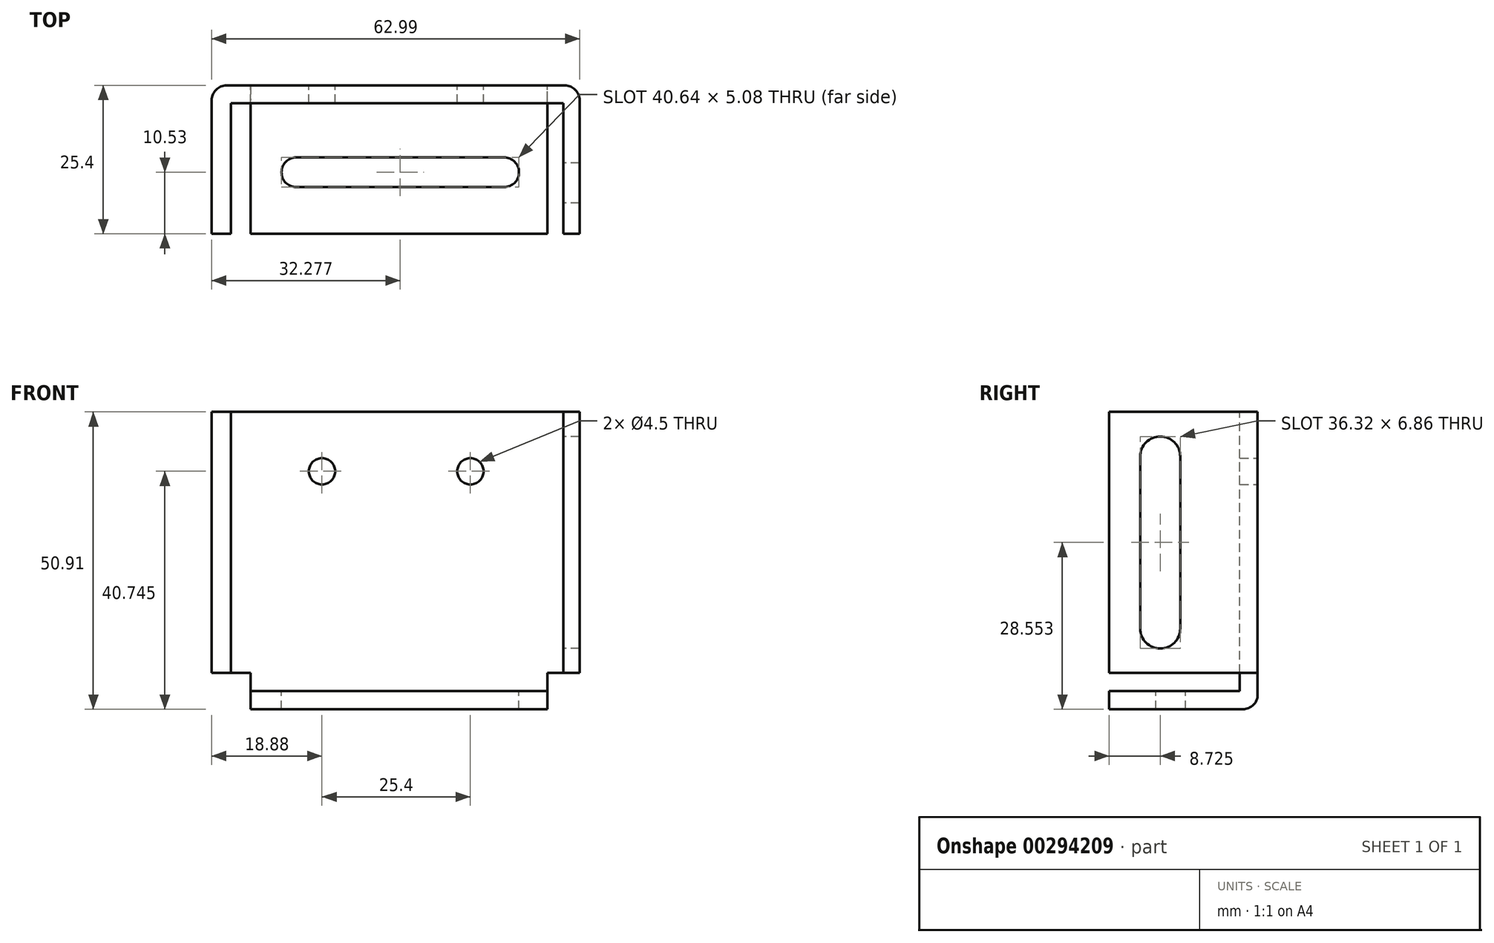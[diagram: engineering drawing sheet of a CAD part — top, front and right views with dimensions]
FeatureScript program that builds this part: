
annotation { "Feature Type Name" : "Feature", "Feature Type Description" : "" }
export const myFeature = defineFeature(function(context is Context, id is Id, definition is map)
    precondition{}
    {
        {
            var Q0;
            Q0=qCreatedBy(makeId("Front.planeOp"),FACE);
            var sketch = newSketch(context, id + "F0", { "sketchPlane" : qUnion([Q0])});
            skLineSegment(sketch, "E0", {"start": v(-29.68, 28.29) * mm, "end": v(33.31, 28.29) * mm});
            skLineSegment(sketch, "E1", {"start": v(33.31, 28.29) * mm, "end": v(33.31, -16.42) * mm});
            skLineSegment(sketch, "E2", {"start": v(33.31, -16.42) * mm, "end": v(27.77, -16.42) * mm});
            skLineSegment(sketch, "E3", {"start": v(27.77, -16.42) * mm, "end": v(27.77, -22.62) * mm});
            skLineSegment(sketch, "E4", {"start": v(27.77, -22.62) * mm, "end": v(-23.03, -22.62) * mm});
            skLineSegment(sketch, "E5", {"start": v(-23.03, -22.62) * mm, "end": v(-23.03, -16.42) * mm});
            skLineSegment(sketch, "E6", {"start": v(-23.03, -16.42) * mm, "end": v(-29.68, -16.42) * mm});
            skLineSegment(sketch, "E7", {"start": v(-29.68, -16.42) * mm, "end": v(-29.68, 28.29) * mm});
            skCircle(sketch, "E8", {"center": v(-10.8, 18.13) * mm, "radius": 2.25 * mm});
            skCircle(sketch, "E9", {"center": v(14.6, 18.13) * mm, "radius": 2.25 * mm});
            skLineSegment(sketch, "E10", {"start": v(-23.03, -19.52) * mm, "end": v(27.77, -19.52) * mm});
            skLineSegment(sketch, "E11", {"start": v(-26.35, -16.42) * mm, "end": v(-26.35, 28.29) * mm});
            skLineSegment(sketch, "E12", {"start": v(30.54, -16.42) * mm, "end": v(30.54, 28.29) * mm});
            skSolve(sketch);
        }
        {
            var Q0;
            Q0=makeQuery(id+"F0.imprint","IMPRINT",FACE,{"disambiguationData":[TD([[makeQuery(id+"F0.imprint","IMPRINT",EDGE,{"derivedFrom":sQuery(id+"F0.wireOp",EDGE,"E8")}),-1.0]])]});
            extrude(context, id + "F1", {"entities" : qUnion([Q0]), "depth" : 3.05 * mm});
        }
        {
            var Q0;
            {var subQ0=sQuery(id+"F0.wireOp",EDGE,"E4");Q0=makeQuery(id+"F0.imprint","IMPRINT",FACE,{"disambiguationData":[TD([[makeQuery(id+"F0.imprint","IMPRINT",EDGE,{"derivedFrom":subQ0}),-1.0]])]});}
            var Q1;
            {var subQ0=sQuery(id+"F0.wireOp",EDGE,"E7");Q1=makeQuery(id+"F0.imprint","IMPRINT",FACE,{"disambiguationData":[TD([[makeQuery(id+"F0.imprint","IMPRINT",EDGE,{"derivedFrom":subQ0}),-1.0]])]});}
            var Q2;
            {var subQ0=sQuery(id+"F0.wireOp",EDGE,"E1");Q2=makeQuery(id+"F0.imprint","IMPRINT",FACE,{"disambiguationData":[TD([[makeQuery(id+"F0.imprint","IMPRINT",EDGE,{"derivedFrom":subQ0}),-1.0]])]});}
            extrude(context, id + "F2", {"entities" : qUnion([Q0, Q1, Q2]), "operationType" : NewBodyOperationType.ADD, "depth" : 25.4 * mm});
        }
        {
            var Q0;
            Q0=makeQuery(id+"F2.opExtrude","SWEPT_FACE",FACE,{"disambiguationData":[OSD([sQuery(id+"F0.wireOp",EDGE,"E10")])]});
            var sketch = newSketch(context, id + "F3", { "sketchPlane" : qUnion([Q0])});
            skLineSegment(sketch, "E13", {"start": v(-15.18, -17.4) * mm, "end": v(20.38, -17.4) * mm});
            skLineSegment(sketch, "E14", {"start": v(-15.18, -12.33) * mm, "end": v(20.38, -12.33) * mm});
            skArc(sketch, "E15", {"start": v(-15.18, -12.33) * mm, "mid": v(-17.72, -14.87) * mm, "end": v(-15.18, -17.4) * mm});
            skArc(sketch, "E16", {"start": v(20.38, -17.4) * mm, "mid": v(22.92, -14.87) * mm, "end": v(20.38, -12.33) * mm});
            skSolve(sketch);
        }
        {
            var Q0;
            Q0=makeQuery(id+"F1.opExtrude","CAP_EDGE",EDGE,{"disambiguationData":[OSD([sQuery(id+"F0.wireOp",EDGE,"E10")])],"isStart":false});
            var Q1;
            Q1=makeQuery(id+"F2.opExtrude","CAP_EDGE",EDGE,{"disambiguationData":[OSD([sQuery(id+"F0.wireOp",EDGE,"E4")])],"isStart":true});
            var Q2;
            Q2=makeQuery(id+"F2.opExtrude","CAP_EDGE",EDGE,{"disambiguationData":[OSD([sQuery(id+"F0.wireOp",EDGE,"E1")])],"isStart":true});
            var Q3;
            Q3=makeQuery(id+"F1.opExtrude","CAP_EDGE",EDGE,{"disambiguationData":[OSD([sQuery(id+"F0.wireOp",EDGE,"E12")])],"isStart":false});
            var Q4;
            Q4=makeQuery(id+"F1.opExtrude","CAP_EDGE",EDGE,{"disambiguationData":[OSD([sQuery(id+"F0.wireOp",EDGE,"E11")])],"isStart":false});
            var Q5;
            Q5=makeQuery(id+"F2.opExtrude","CAP_EDGE",EDGE,{"disambiguationData":[OSD([sQuery(id+"F0.wireOp",EDGE,"E7")])],"isStart":true});
            fillet(context, id + "F4", {"entities" : qUnion([Q0, Q1, Q2, Q3, Q4, Q5]), "radius" : 2.54 * mm, "tangentPropagation" : true, "allowEdgeOverflow" : false});
        }
        {
            var Q0;
            Q0=makeQuery(id+"F2.opExtrude","SWEPT_FACE",FACE,{"disambiguationData":[OSD([sQuery(id+"F0.wireOp",EDGE,"E12")])]});
            var sketch = newSketch(context, id + "F5", { "sketchPlane" : qUnion([Q0])});
            skLineSegment(sketch, "E17", {"start": v(13.25, 20.67) * mm, "end": v(13.25, -8.8) * mm});
            skLineSegment(sketch, "E18", {"start": v(20.1, 20.67) * mm, "end": v(20.1, -8.8) * mm});
            skArc(sketch, "E19", {"start": v(13.25, -8.8) * mm, "mid": v(16.67, -12.23) * mm, "end": v(20.1, -8.8) * mm});
            skArc(sketch, "E20", {"start": v(20.1, 20.67) * mm, "mid": v(16.67, 24.1) * mm, "end": v(13.25, 20.67) * mm});
            skSolve(sketch);
        }
        {
            var Q0;
            Q0=makeQuery(id+"F5.imprint","IMPRINT",FACE,{"disambiguationData":[TD([[makeQuery(id+"F5.imprint","IMPRINT",EDGE,{"derivedFrom":sQuery(id+"F5.wireOp",EDGE,"E17")}),1.0]])]});
            extrude(context, id + "F6", {"entities" : qUnion([Q0]), "operationType" : NewBodyOperationType.REMOVE, "oppositeDirection" : true, "depth" : 25.4 * mm});
        }
        {
            var Q0;
            Q0=makeQuery(id+"F3.imprint","IMPRINT",FACE,{"disambiguationData":[TD([[makeQuery(id+"F3.imprint","IMPRINT",EDGE,{"derivedFrom":sQuery(id+"F3.wireOp",EDGE,"E13")}),1.0]])]});
            extrude(context, id + "F7", {"entities" : qUnion([Q0]), "operationType" : NewBodyOperationType.REMOVE, "oppositeDirection" : true, "depth" : 25.4 * mm});
        }
    });
